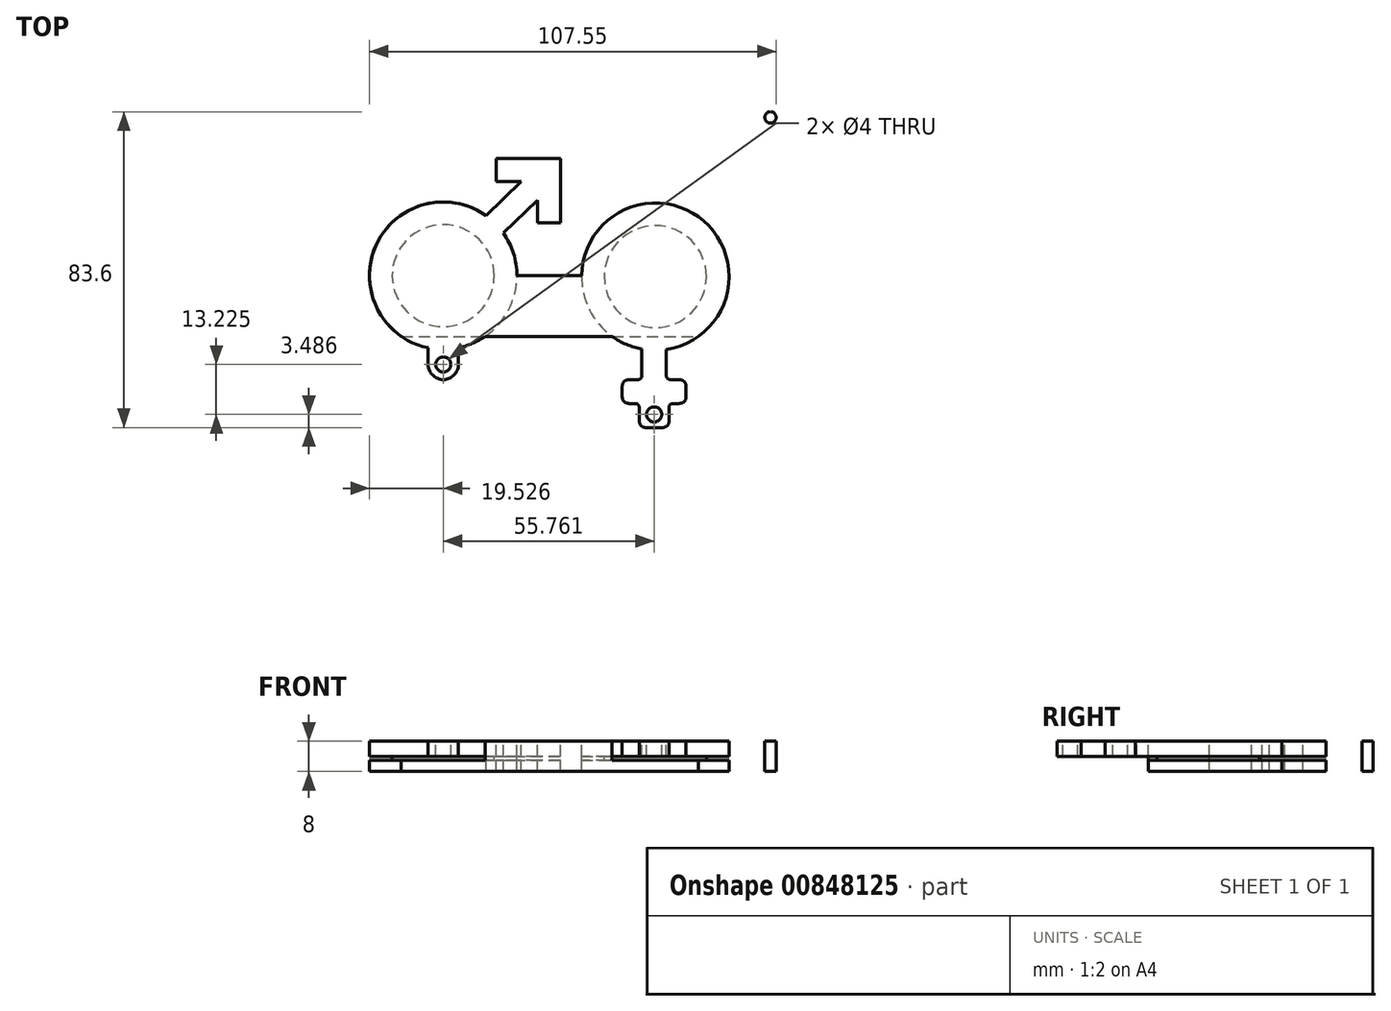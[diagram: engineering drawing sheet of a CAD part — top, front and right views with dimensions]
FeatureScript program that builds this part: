
annotation { "Feature Type Name" : "Feature", "Feature Type Description" : "" }
export const myFeature = defineFeature(function(context is Context, id is Id, definition is map)
    precondition{}
    {
        {
            var Q0;
            Q0=qCreatedBy(makeId("Top.planeOp"),FACE);
            var sketch = newSketch(context, id + "F0", { "sketchPlane" : qUnion([Q0])});
            skLineSegment(sketch, "E0", {"start": v(0, 65) * mm, "end": v(-65, 0) * mm});
            skLineSegment(sketch, "E1", {"start": v(-65, 0) * mm, "end": v(-65, -10) * mm});
            skLineSegment(sketch, "E2", {"start": v(-65, -10) * mm, "end": v(-50, -10) * mm});
            skPoint(sketch, "E3.start.orphan", {"position": v(0, 0) * mm});
            skLineSegment(sketch, "E4.MirrorCS", {"start": v(0, 65) * mm, "end": v(65, 0) * mm});
            skLineSegment(sketch, "E5.MirrorCS", {"start": v(65, 0) * mm, "end": v(65, -10) * mm});
            skLineSegment(sketch, "E6.MirrorCS", {"start": v(65, -10) * mm, "end": v(50, -10) * mm});
            skPoint(sketch, "E7.end.orphan", {"position": v(0, -60) * mm});
            skPoint(sketch, "E7.start.orphan", {"position": v(-55, -60) * mm});
            skPoint(sketch, "E8.MirrorCS.start.orphan", {"position": v(55, -60) * mm});
            skPoint(sketch, "E9.MirrorCS.start.orphan", {"position": v(50, -10) * mm});
            skLineSegment(sketch, "E10", {"start": v(-50, -10) * mm, "end": v(-55, -60) * mm});
            skLineSegment(sketch, "E11", {"start": v(-55, -60) * mm, "end": v(0, -60) * mm});
            skLineSegment(sketch, "E12.MirrorCS", {"start": v(50, -10) * mm, "end": v(55, -60) * mm});
            skLineSegment(sketch, "E13.MirrorCS", {"start": v(55, -60) * mm, "end": v(0, -60) * mm});
            skSolve(sketch);
        }
        {
            var Q0;
            Q0 = qSketchRegion(id + "F0", true);
            extrude(context, id + "F1", {"entities" : qUnion([Q0]), "depth" : 8 * mm, "offsetDistance" : 25 * mm});
        }
        {
            var Q0;
            Q0=makeQuery(id+"F1.opExtrude","SWEPT_EDGE",EDGE,{"disambiguationData":[OSD([sQuery(id+"F0.wireOp",EDGE,"E0"),sQuery(id+"F0.wireOp",EDGE,"E1")])]});
            var Q1;
            Q1=makeQuery(id+"F1.opExtrude","SWEPT_EDGE",EDGE,{"disambiguationData":[OSD([sQuery(id+"F0.wireOp",EDGE,"E4.MirrorCS"),sQuery(id+"F0.wireOp",EDGE,"E5.MirrorCS")])]});
            var Q2;
            Q2=makeQuery(id+"F1.opExtrude","SWEPT_EDGE",EDGE,{"disambiguationData":[OSD([sQuery(id+"F0.wireOp",EDGE,"E0"),sQuery(id+"F0.wireOp",EDGE,"E4.MirrorCS")])]});
            var Q3;
            Q3=makeQuery(id+"F1.opExtrude","SWEPT_EDGE",EDGE,{"disambiguationData":[OSD([sQuery(id+"F0.wireOp",EDGE,"E5.MirrorCS"),sQuery(id+"F0.wireOp",EDGE,"E6.MirrorCS")])]});
            var Q4;
            Q4=makeQuery(id+"F1.opExtrude","SWEPT_EDGE",EDGE,{"disambiguationData":[OSD([sQuery(id+"F0.wireOp",EDGE,"E1"),sQuery(id+"F0.wireOp",EDGE,"E2")])]});
            fillet(context, id + "F2", {"entities" : qUnion([Q0, Q1, Q2, Q3, Q4]), "radius" : 8 * mm, "tangentPropagation" : true, "allowEdgeOverflow" : false});
        }
        {
            var Q0;
            Q0=makeQuery(id+"F1.opExtrude","SWEPT_EDGE",EDGE,{"disambiguationData":[OSD([sQuery(id+"F0.wireOp",EDGE,"E2"),sQuery(id+"F0.wireOp",EDGE,"OkS4Uy9Q-3fJT-eiBS-ctWD-TKyOEgHCFvAM")])]});
            var Q1;
            Q1=makeQuery(id+"F1.opExtrude","SWEPT_EDGE",EDGE,{"disambiguationData":[OSD([sQuery(id+"F0.wireOp",EDGE,"E6.MirrorCS"),sQuery(id+"F0.wireOp",EDGE,"E9.MirrorCS")])]});
            fillet(context, id + "F3", {"entities" : qUnion([Q0, Q1]), "radius" : 1 * mm, "tangentPropagation" : true, "rho" : 0.5, "crossSection" : FilletCrossSection.CONIC, "allowEdgeOverflow" : false});
        }
        {
            var Q0;
            Q0=makeQuery(id+"F1.opExtrude","SWEPT_EDGE",EDGE,{"disambiguationData":[OSD([sQuery(id+"F0.wireOp",EDGE,"E10"),sQuery(id+"F0.wireOp",EDGE,"E11")])]});
            var Q1;
            Q1=makeQuery(id+"F1.opExtrude","SWEPT_EDGE",EDGE,{"disambiguationData":[OSD([sQuery(id+"F0.wireOp",EDGE,"E12.MirrorCS"),sQuery(id+"F0.wireOp",EDGE,"E13.MirrorCS")])]});
            fillet(context, id + "F4", {"entities" : qUnion([Q0, Q1]), "radius" : 8 * mm, "tangentPropagation" : true, "rho" : 0.5, "crossSection" : FilletCrossSection.CONIC, "allowEdgeOverflow" : false});
        }
        {
            var Q0;
            Q0=makeQuery(id+"F1.opExtrude","CAP_FACE",FACE,{"disambiguationData":[OSD([sQuery(id+"F0.wireOp",EDGE,"E0"),sQuery(id+"F0.wireOp",EDGE,"E1"),sQuery(id+"F0.wireOp",EDGE,"E2"),sQuery(id+"F0.wireOp",EDGE,"E4.MirrorCS"),sQuery(id+"F0.wireOp",EDGE,"E5.MirrorCS"),sQuery(id+"F0.wireOp",EDGE,"E6.MirrorCS"),sQuery(id+"F0.wireOp",EDGE,"E10"),sQuery(id+"F0.wireOp",EDGE,"E11"),sQuery(id+"F0.wireOp",EDGE,"E12.MirrorCS"),sQuery(id+"F0.wireOp",EDGE,"E13.MirrorCS")])],"isStart":false});
            var sketch = newSketch(context, id + "F5", { "sketchPlane" : qUnion([Q0])});
            skArc(sketch, "E14", {"start": v(-17.8, -28.08) * mm, "mid": v(-47, -36.13) * mm, "end": v(-33.11, -63.04) * mm});
            skPoint(sketch, "E14.first.point", {"position": v(-28.53, -24.46) * mm});
            skPoint(sketch, "E14.second.point", {"position": v(-47.76, -49.74) * mm});
            skPoint(sketch, "E14.third.point", {"position": v(-10.24, -39.13) * mm});
            skCircle(sketch, "E15", {"center": v(-29.14, -43.95) * mm, "radius": 13.5 * mm});
            skCircle(sketch, "E16", {"center": v(26.97, -44.2) * mm, "radius": 13.5 * mm});
            skArc(sketch, "E17", {"start": v(29.9, -63.48) * mm, "mid": v(27.3, -24.7) * mm, "end": v(23.4, -63.38) * mm});
            skLineSegment(sketch, "E18", {"start": v(23.4, -63.38) * mm, "end": v(23.4, -71.47) * mm});
            skLineSegment(sketch, "E19", {"start": v(23.4, -71.47) * mm, "end": v(18.2, -71.47) * mm});
            skLineSegment(sketch, "E20", {"start": v(18.2, -71.47) * mm, "end": v(18.2, -77.78) * mm});
            skLineSegment(sketch, "E21", {"start": v(18.2, -77.78) * mm, "end": v(22.7, -77.78) * mm});
            skLineSegment(sketch, "E22", {"start": v(22.7, -77.78) * mm, "end": v(22.7, -84.16) * mm});
            skLineSegment(sketch, "E23", {"start": v(29.9, -63.48) * mm, "end": v(29.9, -71.47) * mm});
            skLineSegment(sketch, "E24", {"start": v(29.9, -71.47) * mm, "end": v(35.1, -71.47) * mm});
            skLineSegment(sketch, "E25", {"start": v(35.1, -71.47) * mm, "end": v(35.1, -77.78) * mm});
            skLineSegment(sketch, "E26", {"start": v(35.1, -77.78) * mm, "end": v(30.6, -77.78) * mm});
            skLineSegment(sketch, "E27", {"start": v(30.6, -77.78) * mm, "end": v(30.6, -84.16) * mm});
            skLineSegment(sketch, "E28", {"start": v(22.7, -84.16) * mm, "end": v(30.6, -84.16) * mm});
            skLineSegment(sketch, "E29", {"start": v(-17.8, -28.08) * mm, "end": v(-8.47, -19.1) * mm});
            skLineSegment(sketch, "E30", {"start": v(-8.47, -19.1) * mm, "end": v(-15.14, -19.1) * mm});
            skLineSegment(sketch, "E31", {"start": v(-15.14, -19.1) * mm, "end": v(-15.14, -13) * mm});
            skLineSegment(sketch, "E32", {"start": v(-15.14, -13) * mm, "end": v(1.86, -13) * mm});
            skLineSegment(sketch, "E33", {"start": v(1.86, -13) * mm, "end": v(1.86, -30) * mm});
            skLineSegment(sketch, "E34", {"start": v(1.86, -30) * mm, "end": v(-4.24, -30) * mm});
            skLineSegment(sketch, "E35", {"start": v(-4.24, -30) * mm, "end": v(-4.24, -24.03) * mm});
            skLineSegment(sketch, "E36", {"start": v(-4.24, -24.03) * mm, "end": v(-13.22, -32.69) * mm});
            skLineSegment(sketch, "E37", {"start": v(-29.14, -43.95) * mm, "end": v(26.97, -43.95) * mm});
            skArc(sketch, "E38", {"start": v(-33.11, -67.45) * mm, "mid": v(-29.11, -71.45) * mm, "end": v(-25.11, -67.45) * mm});
            skLineSegment(sketch, "E39.left", {"start": v(-33.11, -67.45) * mm, "end": v(-33.11, -63.04) * mm});
            skLineSegment(sketch, "E39.right", {"start": v(-25.11, -67.45) * mm, "end": v(-25.11, -63.03) * mm});
            skArc(sketch, "E40.trimOffspring", {"start": v(-25.11, -63.03) * mm, "mid": v(-10.98, -51.07) * mm, "end": v(-13.22, -32.69) * mm});
            skCircle(sketch, "E41", {"center": v(-29.11, -67.45) * mm, "radius": 2 * mm});
            skCircle(sketch, "E42", {"center": v(26.65, -80.67) * mm, "radius": 2 * mm});
            skSolve(sketch);
        }
        {
            var Q0;
            Q0=makeQuery(id+"F5.imprint","IMPRINT",FACE,{"disambiguationData":[TD([[makeQuery(id+"F5.imprint","IMPRINT",EDGE,{"derivedFrom":sQuery(id+"F5.wireOp",EDGE,"E15")}),-1.0]])]});
            var Q1;
            Q1=makeQuery(id+"F5.imprint","IMPRINT",FACE,{"disambiguationData":[TD([[makeQuery(id+"F5.imprint","IMPRINT",EDGE,{"derivedFrom":sQuery(id+"F5.wireOp",EDGE,"E38")}),1.0]])]});
            var Q2;
            {var subQ5=sQuery(id+"F5.wireOp",EDGE,"E18");Q2=makeQuery(id+"F5.imprint","IMPRINT",FACE,{"disambiguationData":[TD([[makeQuery(id+"F5.imprint","IMPRINT",EDGE,{"derivedFrom":subQ5}),1.0]])]});}
            var Q3;
            Q3=makeQuery(id+"F5.imprint","IMPRINT",FACE,{"disambiguationData":[TD([[makeQuery(id+"F5.imprint","IMPRINT",EDGE,{"derivedFrom":sQuery(id+"F5.wireOp",EDGE,"E16")}),-1.0]])]});
            extrude(context, id + "F6", {"entities" : qUnion([Q0, Q1, Q2, Q3]), "operationType" : NewBodyOperationType.REMOVE, "oppositeDirection" : true, "depth" : 5 * mm, "offsetDistance" : 25 * mm});
        }
        {
            var Q0;
            Q0 = qSketchRegion(id + "F5", true);
            extrude(context, id + "F7", {"entities" : qUnion([Q0]), "operationType" : NewBodyOperationType.ADD, "oppositeDirection" : true, "depth" : 4 * mm, "offsetDistance" : 25 * mm});
        }
        {
            var Q0;
            Q0=makeQuery(id+"F7.opExtrude","SWEPT_EDGE",EDGE,{"disambiguationData":[OSD([sQuery(id+"F5.wireOp",EDGE,"E27"),sQuery(id+"F5.wireOp",EDGE,"E28")])]});
            var Q1;
            Q1=makeQuery(id+"F7.opExtrude","SWEPT_EDGE",EDGE,{"disambiguationData":[OSD([sQuery(id+"F5.wireOp",EDGE,"E22"),sQuery(id+"F5.wireOp",EDGE,"E28")])]});
            var Q2;
            Q2=makeQuery(id+"F7.opExtrude","SWEPT_EDGE",EDGE,{"disambiguationData":[OSD([sQuery(id+"F5.wireOp",EDGE,"E20"),sQuery(id+"F5.wireOp",EDGE,"E21")])]});
            var Q3;
            Q3=makeQuery(id+"F7.opExtrude","SWEPT_EDGE",EDGE,{"disambiguationData":[OSD([sQuery(id+"F5.wireOp",EDGE,"E25"),sQuery(id+"F5.wireOp",EDGE,"E26")])]});
            var Q4;
            Q4=makeQuery(id+"F7.opExtrude","SWEPT_EDGE",EDGE,{"disambiguationData":[OSD([sQuery(id+"F5.wireOp",EDGE,"E24"),sQuery(id+"F5.wireOp",EDGE,"E25")])]});
            var Q5;
            Q5=makeQuery(id+"F7.opExtrude","SWEPT_EDGE",EDGE,{"disambiguationData":[OSD([sQuery(id+"F5.wireOp",EDGE,"E19"),sQuery(id+"F5.wireOp",EDGE,"E20")])]});
            fillet(context, id + "F8", {"entities" : qUnion([Q0, Q1, Q2, Q3, Q4, Q5]), "radius" : 2 * mm, "tangentPropagation" : true, "rho" : 0.5, "crossSection" : FilletCrossSection.CONIC, "allowEdgeOverflow" : false});
        }
        {
            var Q0;
            Q0=makeQuery(id+"F7.opExtrude","SWEPT_EDGE",EDGE,{"disambiguationData":[OSD([sQuery(id+"F5.wireOp",EDGE,"E19"),sQuery(id+"F5.wireOp",EDGE,"E20")])]});
            var Q1;
            Q1=makeQuery(id+"F7.opExtrude","SWEPT_EDGE",EDGE,{"disambiguationData":[OSD([sQuery(id+"F5.wireOp",EDGE,"E20"),sQuery(id+"F5.wireOp",EDGE,"E21")])]});
            var Q2;
            Q2=makeQuery(id+"F7.opExtrude","SWEPT_EDGE",EDGE,{"disambiguationData":[OSD([sQuery(id+"F5.wireOp",EDGE,"E22"),sQuery(id+"F5.wireOp",EDGE,"E28")])]});
            var Q3;
            Q3=makeQuery(id+"F7.opExtrude","SWEPT_EDGE",EDGE,{"disambiguationData":[OSD([sQuery(id+"F5.wireOp",EDGE,"E27"),sQuery(id+"F5.wireOp",EDGE,"E28")])]});
            var Q4;
            Q4=makeQuery(id+"F7.opExtrude","SWEPT_EDGE",EDGE,{"disambiguationData":[OSD([sQuery(id+"F5.wireOp",EDGE,"E25"),sQuery(id+"F5.wireOp",EDGE,"E26")])]});
            var Q5;
            Q5=makeQuery(id+"F7.opExtrude","SWEPT_EDGE",EDGE,{"disambiguationData":[OSD([sQuery(id+"F5.wireOp",EDGE,"E24"),sQuery(id+"F5.wireOp",EDGE,"E25")])]});
            var Q6;
            Q6=makeQuery(id+"F7.opExtrude","SWEPT_EDGE",EDGE,{"disambiguationData":[OSD([sQuery(id+"F5.wireOp",EDGE,"E18"),sQuery(id+"F5.wireOp",EDGE,"E19")])]});
            var Q7;
            Q7=makeQuery(id+"F7.opExtrude","SWEPT_EDGE",EDGE,{"disambiguationData":[OSD([sQuery(id+"F5.wireOp",EDGE,"E23"),sQuery(id+"F5.wireOp",EDGE,"E24")])]});
            var Q8;
            Q8=makeQuery(id+"F7.opExtrude","SWEPT_EDGE",EDGE,{"disambiguationData":[OSD([sQuery(id+"F5.wireOp",EDGE,"E26"),sQuery(id+"F5.wireOp",EDGE,"E27")])]});
            var Q9;
            Q9=makeQuery(id+"F7.opExtrude","SWEPT_EDGE",EDGE,{"disambiguationData":[OSD([sQuery(id+"F5.wireOp",EDGE,"E21"),sQuery(id+"F5.wireOp",EDGE,"E22")])]});
            fillet(context, id + "F9", {"entities" : qUnion([Q0, Q1, Q2, Q3, Q4, Q5, Q6, Q7, Q8, Q9]), "radius" : 1 * mm, "tangentPropagation" : true, "allowEdgeOverflow" : false});
        }
        {
            var Q0;
            {var subQ17=sQuery(id+"F5.wireOp",EDGE,"E29");Q0=makeQuery(id+"F5.imprint","IMPRINT",FACE,{"disambiguationData":[TD([[makeQuery(id+"F5.imprint","IMPRINT",EDGE,{"derivedFrom":subQ17}),1.0]])]});}
            var sketch = newSketch(context, id + "F10", { "sketchPlane" : qUnion([Q0])});
            skCircle(sketch, "E43", {"center": v(-57.4, -2.06) * mm, "radius": 1.5 * mm});
            skCircle(sketch, "E44.MirrorC", {"center": v(57.4, -2.06) * mm, "radius": 1.5 * mm});
            skSolve(sketch);
        }
        {
            var Q0;
            Q0=makeQuery(id+"F10.imprint","IMPRINT",FACE,{"disambiguationData":[TD([[makeQuery(id+"F10.imprint","IMPRINT",EDGE,{"derivedFrom":sQuery(id+"F10.wireOp",EDGE,"E43")}),1.0]])]});
            var Q1;
            Q1=makeQuery(id+"F10.imprint","IMPRINT",FACE,{"disambiguationData":[TD([[makeQuery(id+"F10.imprint","IMPRINT",EDGE,{"derivedFrom":sQuery(id+"F10.wireOp",EDGE,"E44.MirrorC")}),-1.0]])]});
            extrude(context, id + "F11", {"entities" : qUnion([Q0, Q1]), "operationType" : NewBodyOperationType.REMOVE, "oppositeDirection" : true, "depth" : 25 * mm, "offsetDistance" : 25 * mm});
        }
    });
